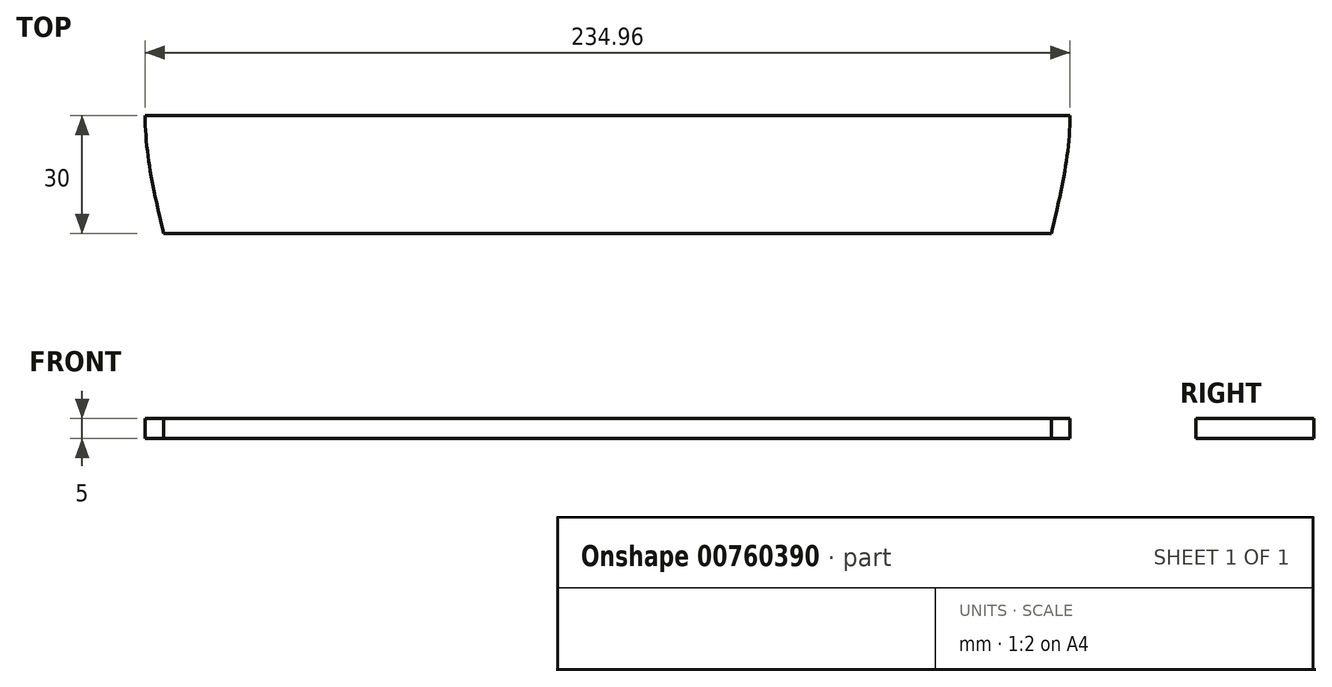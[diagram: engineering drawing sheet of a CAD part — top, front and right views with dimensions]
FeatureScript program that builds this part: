
annotation { "Feature Type Name" : "Feature", "Feature Type Description" : "" }
export const myFeature = defineFeature(function(context is Context, id is Id, definition is map)
    precondition{}
    {
        {
            var Q0;
            Q0=qCreatedBy(makeId("Top.planeOp"),FACE);
            var sketch = newSketch(context, id + "F0", { "sketchPlane" : qUnion([Q0])});
            skPoint(sketch, "E0", {"position": v(120.55, -132.94) * mm});
            skPoint(sketch, "E1", {"position": v(86.1, -177.7) * mm});
            skPoint(sketch, "E2", {"position": v(55.36, -169.8) * mm});
            skPoint(sketch, "E3", {"position": v(0, -197.44) * mm});
            skPoint(sketch, "E4", {"position": v(110.71, -142.15) * mm});
            skPoint(sketch, "E5", {"position": v(117.48, 0) * mm});
            skPoint(sketch, "E6", {"position": v(106.4, -66.47) * mm});
            skLineSegment(sketch, "E7", {"start": v(0, 292) * mm, "end": v(0, -197.44) * mm, "construction": true});
            skPoint(sketch, "E8.MirrorP", {"position": v(-117.48, 0) * mm});
            skPoint(sketch, "E9.MirrorP", {"position": v(-106.4, -66.47) * mm});
            skPoint(sketch, "E10.MirrorP", {"position": v(-120.55, -132.94) * mm});
            skPoint(sketch, "E11.MirrorP", {"position": v(-110.71, -142.15) * mm});
            skPoint(sketch, "E12.MirrorP", {"position": v(-86.1, -177.7) * mm});
            skPoint(sketch, "E13.MirrorP", {"position": v(-55.36, -169.8) * mm});
            skPoint(sketch, "E14", {"position": v(0, 0) * mm});
            skPoint(sketch, "E15", {"position": v(-117.3, -129.45) * mm});
            skPoint(sketch, "E16", {"position": v(-109.77, -151.8) * mm});
            skPoint(sketch, "E17", {"position": v(-117.3, -138.2) * mm});
            skPoint(sketch, "E18", {"position": v(-105.1, -168.47) * mm});
            skPoint(sketch, "E19", {"position": v(-76.04, -175.14) * mm});
            skPoint(sketch, "E20", {"position": v(-48.6, -178.72) * mm});
            skPoint(sketch, "E21", {"position": v(-53.93, -172.02) * mm});
            skPoint(sketch, "E22", {"position": v(-58.13, -168.59) * mm});
            skPoint(sketch, "E23", {"position": v(-95.73, -175.68) * mm});
            skPoint(sketch, "E24", {"position": v(-120.2, -134.48) * mm});
            skPoint(sketch, "E25.MirrorP", {"position": v(48.6, -178.72) * mm});
            skPoint(sketch, "E26.MirrorP", {"position": v(53.93, -172.02) * mm});
            skPoint(sketch, "E27.MirrorP", {"position": v(58.13, -168.59) * mm});
            skPoint(sketch, "E28.MirrorP", {"position": v(76.04, -175.14) * mm});
            skPoint(sketch, "E29.MirrorP", {"position": v(95.73, -175.68) * mm});
            skPoint(sketch, "E30.MirrorP", {"position": v(109.77, -151.8) * mm});
            skPoint(sketch, "E31.MirrorP", {"position": v(117.3, -138.2) * mm});
            skPoint(sketch, "E32.MirrorP", {"position": v(120.2, -134.48) * mm});
            skPoint(sketch, "E33.MirrorP", {"position": v(117.3, -129.45) * mm});
            skPoint(sketch, "E34", {"position": v(-112.06, -140.6) * mm});
            skPoint(sketch, "E35.MirrorP", {"position": v(105.1, -168.47) * mm});
            skPoint(sketch, "E36.MirrorP", {"position": v(-106.4, 66.47) * mm});
            skPoint(sketch, "E37.MirrorP", {"position": v(-112.06, 140.6) * mm});
            skPoint(sketch, "E38.MirrorP", {"position": v(-120.55, 132.94) * mm});
            skPoint(sketch, "E39.MirrorP", {"position": v(55.36, 169.8) * mm});
            skPoint(sketch, "E40.MirrorP", {"position": v(120.55, 132.94) * mm});
            skPoint(sketch, "E41.MirrorP", {"position": v(-53.93, 172.02) * mm});
            skPoint(sketch, "E42.MirrorP", {"position": v(105.1, 168.47) * mm});
            skPoint(sketch, "E43.MirrorP", {"position": v(48.6, 178.72) * mm});
            skPoint(sketch, "E44.MirrorP", {"position": v(95.73, 175.68) * mm});
            skPoint(sketch, "E45.MirrorP", {"position": v(109.77, 151.8) * mm});
            skPoint(sketch, "E46.MirrorP", {"position": v(-58.13, 168.59) * mm});
            skPoint(sketch, "E47.MirrorP", {"position": v(-110.71, 142.15) * mm});
            skPoint(sketch, "E48.MirrorP", {"position": v(-55.36, 169.8) * mm});
            skPoint(sketch, "E49.MirrorP", {"position": v(58.13, 168.59) * mm});
            skPoint(sketch, "E50.MirrorP", {"position": v(-117.3, 129.45) * mm});
            skPoint(sketch, "E51.MirrorP", {"position": v(-109.77, 151.8) * mm});
            skPoint(sketch, "E52.MirrorP", {"position": v(110.71, 142.15) * mm});
            skPoint(sketch, "E53.MirrorP", {"position": v(53.93, 172.02) * mm});
            skPoint(sketch, "E54.MirrorP", {"position": v(-120.2, 134.48) * mm});
            skPoint(sketch, "E55.MirrorP", {"position": v(120.2, 134.48) * mm});
            skPoint(sketch, "E56.MirrorP", {"position": v(-86.1, 177.7) * mm});
            skPoint(sketch, "E57.MirrorP", {"position": v(-76.04, 175.14) * mm});
            skPoint(sketch, "E58.MirrorP", {"position": v(117.3, 138.2) * mm});
            skPoint(sketch, "E59.MirrorP", {"position": v(86.1, 177.7) * mm});
            skPoint(sketch, "E60.MirrorP", {"position": v(-105.1, 168.47) * mm});
            skPoint(sketch, "E61.MirrorP", {"position": v(76.04, 175.14) * mm});
            skPoint(sketch, "E62.MirrorP", {"position": v(117.3, 129.45) * mm});
            skPoint(sketch, "E63.MirrorP", {"position": v(0, 197.44) * mm});
            skPoint(sketch, "E64.MirrorP", {"position": v(-117.3, 138.2) * mm});
            skPoint(sketch, "E65.MirrorP", {"position": v(-95.73, 175.68) * mm});
            skPoint(sketch, "E66.MirrorP", {"position": v(-48.6, 178.72) * mm});
            skPoint(sketch, "E67.MirrorP", {"position": v(106.4, 66.47) * mm});
            skFitSpline(sketch, "E68", {"points": [v(-117.48, 0) * mm, v(-106.4, 66.47) * mm, v(-117.3, 129.45) * mm, v(-120.55, 132.94) * mm, v(-120.2, 134.48) * mm, v(-117.3, 138.2) * mm, v(-112.06, 140.6) * mm, v(-110.71, 142.15) * mm, v(-109.77, 151.8) * mm, v(-105.1, 168.47) * mm, v(-95.73, 175.68) * mm, v(-86.1, 177.7) * mm, v(-76.04, 175.14) * mm, v(-58.13, 168.59) * mm, v(-55.36, 169.8) * mm, v(-53.93, 172.02) * mm, v(-48.6, 178.72) * mm, v(0, 197.44) * mm, v(48.6, 178.72) * mm, v(53.93, 172.02) * mm, v(55.36, 169.8) * mm, v(58.13, 168.59) * mm, v(76.04, 175.14) * mm, v(86.1, 177.7) * mm, v(95.73, 175.68) * mm, v(105.1, 168.47) * mm, v(109.77, 151.8) * mm, v(110.71, 142.15) * mm, v(117.3, 138.2) * mm, v(120.2, 134.48) * mm, v(120.55, 132.94) * mm, v(117.3, 129.45) * mm, v(106.4, 66.47) * mm, v(117.48, 0) * mm, v(106.4, -66.47) * mm, v(117.3, -129.45) * mm, v(120.55, -132.94) * mm, v(120.2, -134.48) * mm, v(117.3, -138.2) * mm, v(110.71, -142.15) * mm, v(109.77, -151.8) * mm, v(105.1, -168.47) * mm, v(95.73, -175.68) * mm, v(86.1, -177.7) * mm, v(76.04, -175.14) * mm, v(58.13, -168.59) * mm, v(55.36, -169.8) * mm, v(53.93, -172.02) * mm, v(48.6, -178.72) * mm, v(0, -197.44) * mm, v(-48.6, -178.72) * mm, v(-53.93, -172.02) * mm, v(-55.36, -169.8) * mm, v(-58.13, -168.59) * mm, v(-76.04, -175.14) * mm, v(-86.1, -177.7) * mm, v(-95.73, -175.68) * mm, v(-105.1, -168.47) * mm, v(-109.77, -151.8) * mm, v(-110.71, -142.15) * mm, v(-112.06, -140.6) * mm, v(-117.3, -138.2) * mm, v(-120.2, -134.48) * mm, v(-120.55, -132.94) * mm, v(-117.3, -129.45) * mm, v(-106.4, -66.47) * mm, v(-117.48, 0) * mm]});
            skPoint(sketch, "E69", {"position": v(0, 295) * mm});
            skPoint(sketch, "E70", {"position": v(-30, 295) * mm});
            skPoint(sketch, "E71", {"position": v(-225, 0) * mm});
            skPoint(sketch, "E72", {"position": v(-225, 100) * mm});
            skPoint(sketch, "E73.MirrorP", {"position": v(225, 100) * mm});
            skPoint(sketch, "E74.MirrorP", {"position": v(225, -60) * mm});
            skLineSegment(sketch, "E75", {"start": v(0, 0) * mm, "end": v(-373.3, 215.53) * mm, "construction": true});
            skLineSegment(sketch, "E76", {"start": v(0, 0) * mm, "end": v(-204.64, 354.44) * mm, "construction": true});
            skLineSegment(sketch, "E77", {"start": v(-225, 0) * mm, "end": v(-225, 100) * mm});
            skLineSegment(sketch, "E78", {"start": v(-30, 295) * mm, "end": v(0, 295) * mm});
            skPoint(sketch, "E79", {"position": v(-30, 100) * mm});
            skArc(sketch, "E80", {"start": v(-30, 295) * mm, "mid": v(-167.89, 237.89) * mm, "end": v(-225, 100) * mm});
            skLineSegment(sketch, "E81.MirrorCS", {"start": v(225, 0) * mm, "end": v(225, 100) * mm});
            skArc(sketch, "E82.MirrorCS", {"start": v(30, 295) * mm, "mid": v(167.89, 237.89) * mm, "end": v(225, 100) * mm});
            skLineSegment(sketch, "E83.MirrorCS", {"start": v(30, 295) * mm, "end": v(0, 295) * mm});
            skArc(sketch, "E84.MirrorCS", {"start": v(-30, -295) * mm, "mid": v(-167.89, -237.89) * mm, "end": v(-225, -100) * mm});
            skLineSegment(sketch, "E85.MirrorCS", {"start": v(-225, 0) * mm, "end": v(-225, -100) * mm});
            skLineSegment(sketch, "E86.MirrorCS", {"start": v(225, 0) * mm, "end": v(225, -100) * mm});
            skArc(sketch, "E87.MirrorCS", {"start": v(30, -295) * mm, "mid": v(167.89, -237.89) * mm, "end": v(225, -100) * mm});
            skLineSegment(sketch, "E88.MirrorCS", {"start": v(30, -295) * mm, "end": v(0, -295) * mm});
            skLineSegment(sketch, "E89.MirrorCS", {"start": v(-30, -295) * mm, "end": v(0, -295) * mm});
            skLineSegment(sketch, "E90", {"start": v(-254.05, 0) * mm, "end": v(241.92, 0) * mm});
            skLineSegment(sketch, "E91.0", {"start": v(-254.05, -30) * mm, "end": v(-225, -30) * mm});
            skLineSegment(sketch, "E92.trimOffspring", {"start": v(-112.75, -30) * mm, "end": v(112.75, -30) * mm});
            skLineSegment(sketch, "E93.trimOffspring", {"start": v(225, -30) * mm, "end": v(241.92, -30) * mm});
            skSolve(sketch);
        }
        {
            var Q0;
            Q0=makeQuery(id+"F0.imprint","IMPRINT",FACE,{"disambiguationData":[TD([[makeQuery(id+"F0.imprint","IMPRINT",EDGE,{"derivedFrom":sQuery(id+"F0.wireOp",EDGE,"E68")}),-1.0]])]});
            extrude(context, id + "F1", {"entities" : qUnion([Q0]), "endBound" : BoundingType.SYMMETRIC, "depth" : 5 * mm, "offsetDistance" : 25 * mm});
        }
        {
            var Q0;
            Q0=makeQuery(id+"F1.opExtrude","CAP_FACE",FACE,{"disambiguationData":[OSD([sQuery(id+"F0.wireOp",EDGE,"E68"),sQuery(id+"F0.wireOp",EDGE,"E92.trimOffspring")])],"isStart":false});
            cPlane(context, id + "F2", {"entities" : qUnion([Q0]), "cplaneType" : CPlaneType.OFFSET, "offset" : 50 * mm, "width" : 150 * mm, "height" : 150 * mm});
        }
    });
